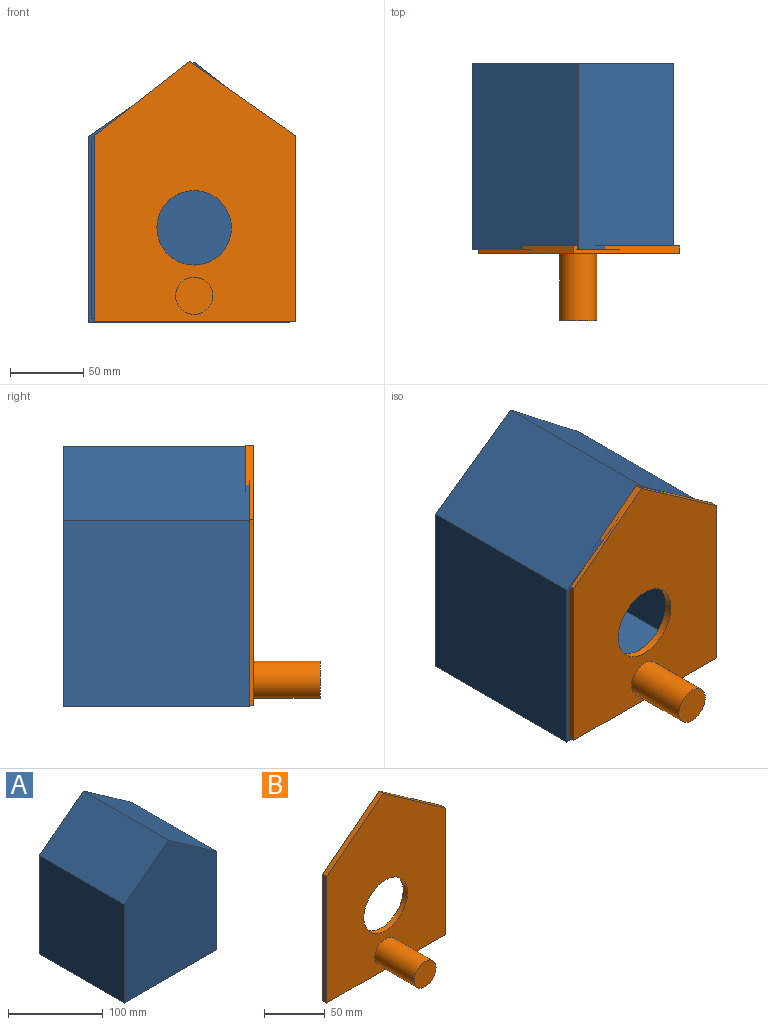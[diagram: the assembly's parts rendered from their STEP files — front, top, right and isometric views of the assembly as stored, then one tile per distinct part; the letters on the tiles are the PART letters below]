
ASSEMBLY  parts=2 mates=1
PART A: 13 faces, bbox 137.8x127x177.8 mm
  f0: plane 127x127mm, normal (1,0,0), area 16129mm2, adj f1,f4,f5,f6
  f1: plane 127x72.38mm, normal (0.57,0,0.82), area 11230.8mm2, adj f0,f2,f5,f6
  f2: plane 127x65.44mm, normal (-0.61,0,0.79), area 10520.9mm2, adj f1,f3,f5,f6
  f3: plane 127x127mm, normal (-1,0,0), area 16129mm2, adj f2,f4,f5,f6
  f4: plane 137.82x127mm, normal (0,0,-1), area 17503.4mm2, adj f0,f3,f5,f6
  f5: plane 177.8x137.82mm, normal (0,-1,0), area 21004.1mm2, adj f0,f1,f2,f3,f4
  f6: plane 177.8x137.82mm, normal (0,1,0), area 1406.1mm2, adj f0,f1,f2,f3,f4,f7,f8,f9
  f7: plane 124.46x123.14mm, normal (-1,0,0), area 15325.9mm2, adj f6,f8,f11,f12
  f8: plane 124.46x69.77mm, normal (-0.57,0,-0.82), area 10608.4mm2, adj f6,f7,f9,f12
  f9: plane 124.46x62.97mm, normal (0.61,0,-0.79), area 9922.3mm2, adj f6,f8,f10,f12
  f10: plane 124.46x123.22mm, normal (1,0,0), area 15335.5mm2, adj f6,f9,f11,f12
  f11: plane 132.74x124.46mm, normal (0,0,1), area 16521.1mm2, adj f6,f7,f10,f12
  f12: plane 172.1x132.74mm, normal (0,1,0), area 19598mm2, adj f7,f8,f9,f10,f11
PART B: 10 faces, bbox 137.8x50.8x177.8 mm
  f0: cylinder r=12.7mm len=45.72mm, axis (0,1,0), area 3648.3mm2, adj f1,f8
  f1: plane 25.4x25.4mm, normal (0,-1,0), area 506.7mm2, adj f0
  f2: plane 65.44x50.8mm, normal (-0.61,0,0.79), area 420.8mm2, adj f3,f6,f8,f9
  f3: plane 127x5.08mm, normal (-1,0,0), area 645.2mm2, adj f2,f4,f8,f9
  f4: plane 137.82x5.08mm, normal (0,0,-1), area 700.1mm2, adj f3,f5,f8,f9
  f5: plane 127x5.08mm, normal (1,0,0), area 645.2mm2, adj f4,f6,f8,f9
  f6: plane 72.38x50.8mm, normal (0.57,0,0.82), area 449.2mm2, adj f2,f5,f8,f9
  f7: cylinder r=25.4mm len=50.8mm, axis (0,1,0), area 810.7mm2, adj f8,f9
  f8: plane 177.8x137.82mm, normal (0,-1,0), area 18470.5mm2, adj f0,f2,f3,f4,f5,f6,f7
  f9: plane 177.8x137.82mm, normal (0,1,0), area 18977.2mm2, adj f2,f3,f4,f5,f6,f7
PLACE A rot(axis=(0,0,1),180deg) t=(58.07,-252.61,-55.68)mm
PLACE B t=(-7.31,-250.07,38.06)mm
MATE slider B.f3 <-> A.f7  axis (-1,0,0) through (-75.65,-252.61,8.43)mm
